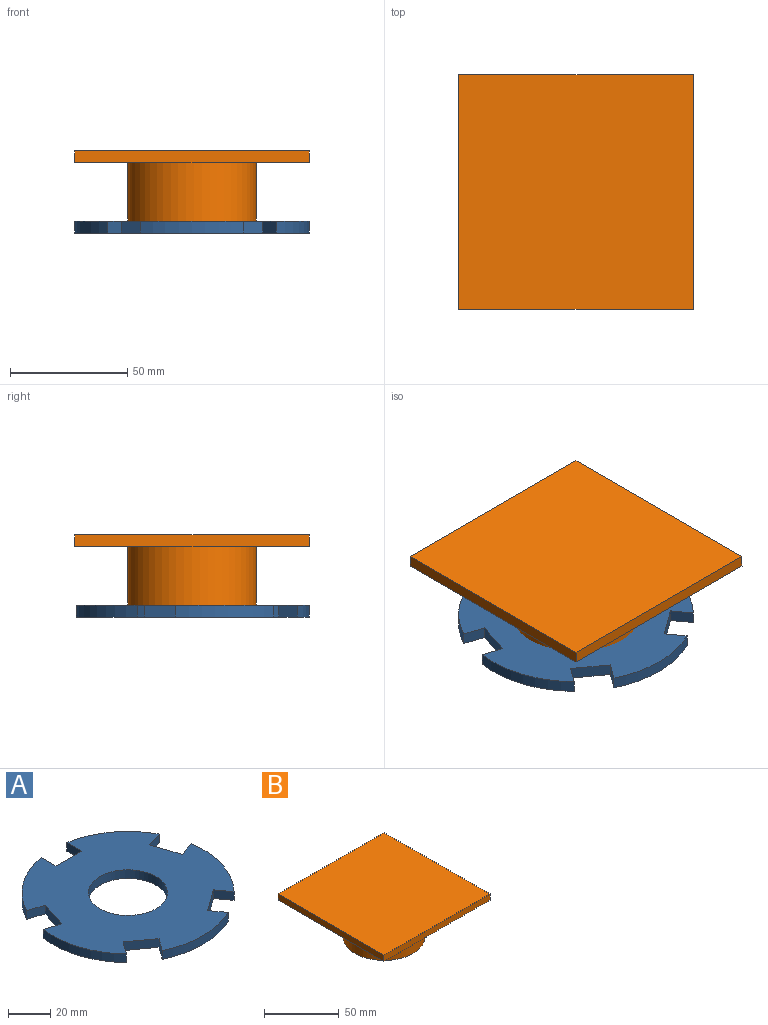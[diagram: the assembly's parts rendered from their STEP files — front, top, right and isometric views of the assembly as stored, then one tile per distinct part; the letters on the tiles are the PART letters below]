
ASSEMBLY  parts=2 mates=1
PART A: 23 faces, bbox 100x99.3x5 mm
  f0: cylinder r=50mm len=35.62mm, axis (0,0,-1), area 227.9mm2, adj f2,f17,f18,f22
  f1: plane 9.38x5mm, normal (-0.31,0.95,0), area 49.3mm2, adj f3,f4,f17,f18
  f2: plane 9.38x5mm, normal (0.31,-0.95,0), area 49.3mm2, adj f0,f3,f17,f18
  f3: plane 16.32x5.3mm, normal (0.95,0.31,0), area 85.8mm2, adj f1,f2,f17,f18
  f4: cylinder r=50mm len=41.87mm, axis (0,0,-1), area 227.9mm2, adj f1,f6,f17,f18
  f5: plane 7.98x5.8mm, normal (0.81,0.59,0), area 49.3mm2, adj f7,f8,f17,f18
  f6: plane 7.98x5.8mm, normal (-0.81,-0.59,0), area 49.3mm2, adj f4,f7,f17,f18
  f7: plane 13.88x10.09mm, normal (0.59,-0.81,0), area 85.8mm2, adj f5,f6,f17,f18
  f8: cylinder r=50mm len=44.03mm, axis (0,0,-1), area 227.9mm2, adj f5,f10,f17,f18
  f9: plane 7.98x5.8mm, normal (0.81,-0.59,0), area 49.3mm2, adj f11,f12,f17,f18
  f10: plane 7.98x5.8mm, normal (-0.81,0.59,0), area 49.3mm2, adj f8,f11,f17,f18
  f11: plane 13.88x10.09mm, normal (-0.59,-0.81,0), area 85.8mm2, adj f9,f10,f17,f18
  f12: cylinder r=50mm len=41.87mm, axis (0,0,-1), area 227.9mm2, adj f9,f14,f17,f18
  f13: plane 9.38x5mm, normal (-0.31,-0.95,0), area 49.3mm2, adj f15,f16,f17,f18
  f14: plane 9.38x5mm, normal (0.31,0.95,0), area 49.3mm2, adj f12,f15,f17,f18
  f15: plane 16.32x5.3mm, normal (-0.95,0.31,0), area 85.8mm2, adj f13,f14,f17,f18
  f16: cylinder r=50mm len=35.62mm, axis (0,0,-1), area 227.9mm2, adj f13,f17,f18,f20
  f17: plane 100x99.26mm, normal (0,0,1), area 5871.2mm2, adj f0,f1,f2,f3,f4,f5,f6,f7
  f18: plane 100x99.26mm, normal (0,0,-1), area 5871.2mm2, adj f0,f1,f2,f3,f4,f5,f6,f7
  f19: cylinder r=18.66mm len=37.32mm, axis (0,0,1), area 586.2mm2, adj f17,f18
  f20: plane 9.87x5mm, normal (1,0,0), area 49.3mm2, adj f16,f17,f18,f21
  f21: plane 17.16x5mm, normal (0,1,0), area 85.8mm2, adj f17,f18,f20,f22
  f22: plane 9.87x5mm, normal (-1,0,0), area 49.3mm2, adj f0,f17,f18,f21
PART B: 8 faces, bbox 100x100x35 mm
  f0: plane 100x5mm, normal (0,-1,0), area 500mm2, adj f1,f3,f4,f5
  f1: plane 100x5mm, normal (1,0,0), area 500mm2, adj f0,f2,f4,f5
  f2: plane 100x5mm, normal (0,1,0), area 500mm2, adj f1,f3,f4,f5
  f3: plane 100x5mm, normal (-1,0,0), area 500mm2, adj f0,f2,f4,f5
  f4: plane 100x100mm, normal (0,0,-1), area 7649.3mm2, adj f0,f1,f2,f3,f6
  f5: plane 100x100mm, normal (0,0,1), area 10000mm2, adj f0,f1,f2,f3
  f6: cylinder r=27.35mm len=54.71mm, axis (0,0,1), area 5156.1mm2, adj f4,f7
  f7: plane 54.71x54.71mm, normal (0,0,-1), area 2350.7mm2, adj f6
PLACE A t=(71.79,-106.77,-27.31)mm
PLACE B t=(71.79,-106.77,7.69)mm
MATE revolute A.f19 <-> B.f6  axis (0,0,-1) through (71.79,-106.77,-27.31)mm
